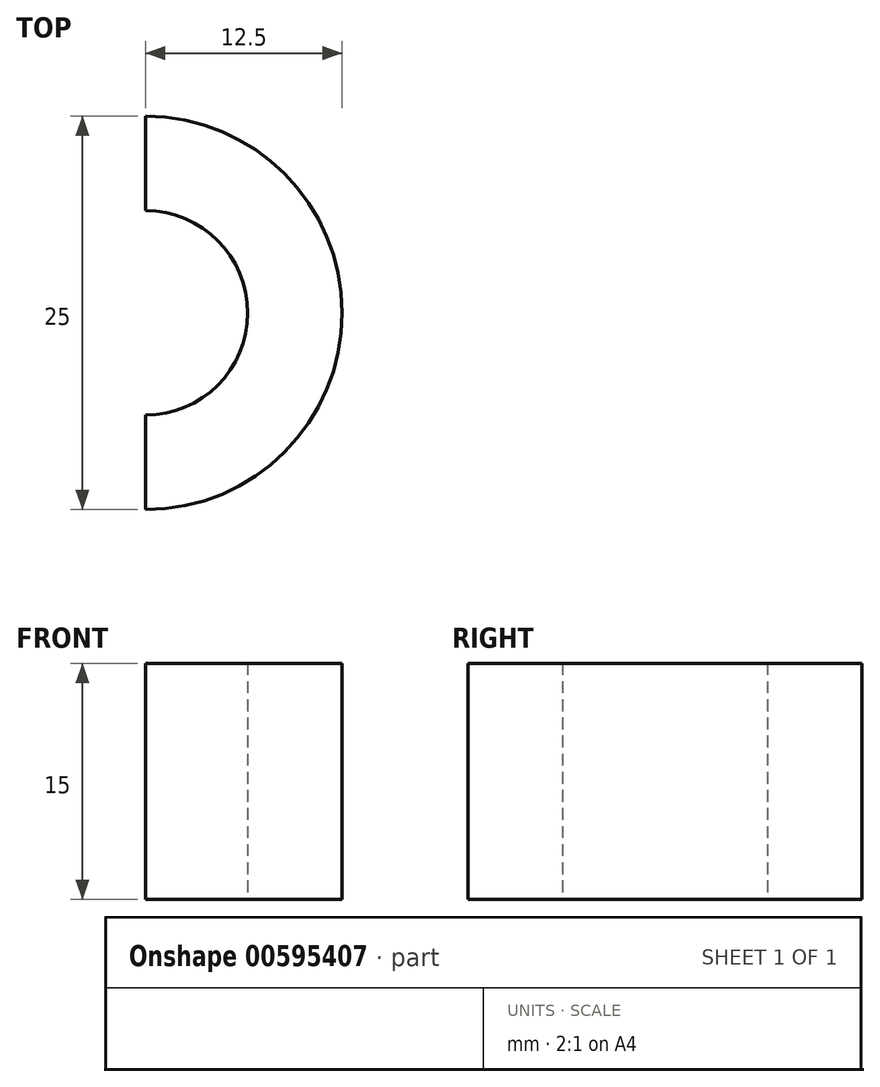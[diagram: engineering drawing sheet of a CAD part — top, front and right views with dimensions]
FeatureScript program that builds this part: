
annotation { "Feature Type Name" : "Feature", "Feature Type Description" : "" }
export const myFeature = defineFeature(function(context is Context, id is Id, definition is map)
    precondition{}
    {
        {
            var Q0;
            Q0=qCreatedBy(makeId("Top.planeOp"),FACE);
            var sketch = newSketch(context, id + "F0", { "sketchPlane" : qUnion([Q0])});
            skArc(sketch, "E0", {"start": v(0, 12.5) * mm, "mid": v(12.5, 0) * mm, "end": v(0, -12.5) * mm});
            skArc(sketch, "E1", {"start": v(0, 6.5) * mm, "mid": v(6.5, 0) * mm, "end": v(0, -6.5) * mm});
            skLineSegment(sketch, "E2", {"start": v(0, 12.5) * mm, "end": v(0, 6.5) * mm});
            skLineSegment(sketch, "E3", {"start": v(0, -6.5) * mm, "end": v(0, -12.5) * mm});
            skSolve(sketch);
        }
        {
            var Q0;
            Q0 = qSketchRegion(id + "F0", true);
            extrude(context, id + "F1", {"entities" : qUnion([Q0]), "depth" : 15 * mm, "offsetDistance" : 25 * mm});
        }
    });
